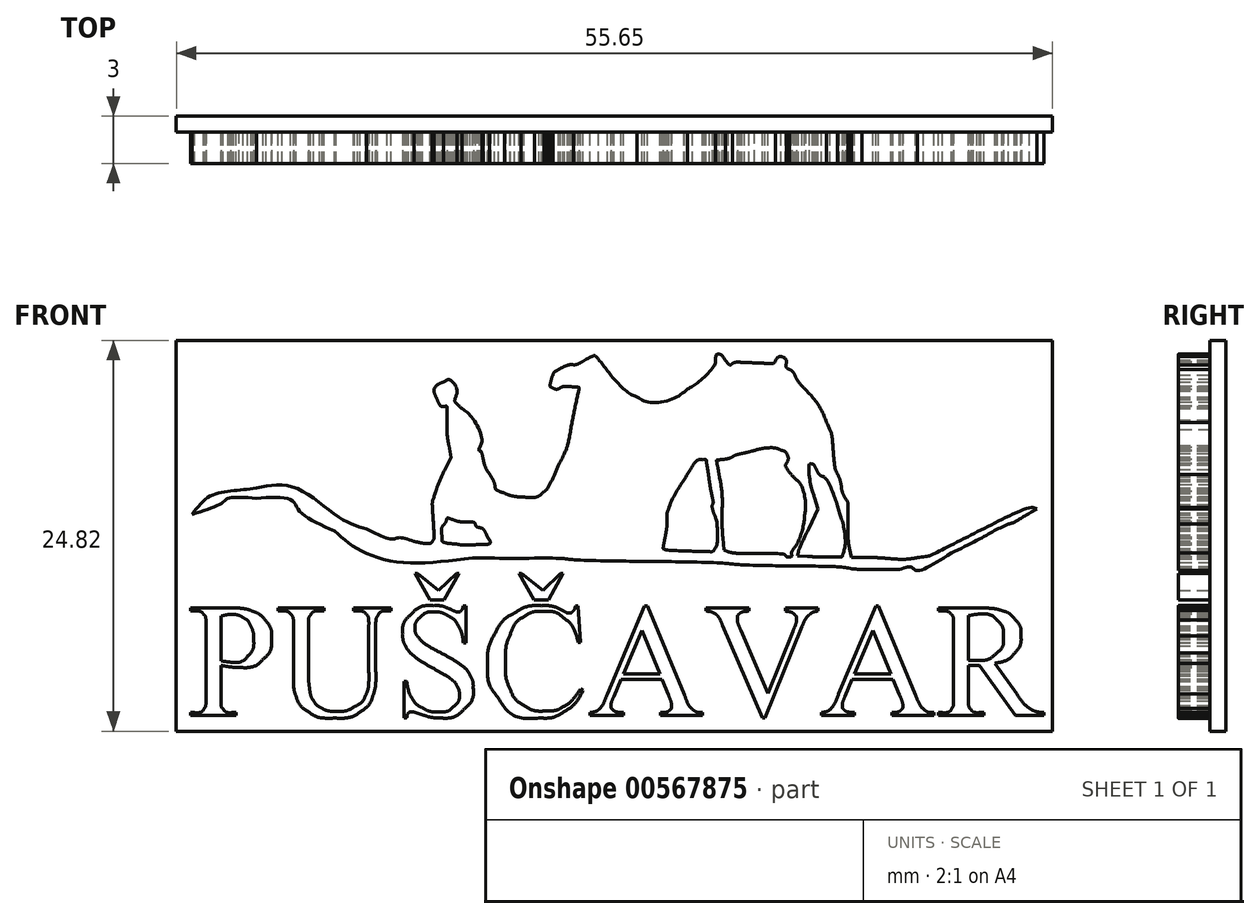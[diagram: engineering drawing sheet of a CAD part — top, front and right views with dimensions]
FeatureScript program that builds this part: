
annotation { "Feature Type Name" : "Feature", "Feature Type Description" : "" }
export const myFeature = defineFeature(function(context is Context, id is Id, definition is map)
    precondition{}
    {
        {
            var Q0;
            Q0=qCreatedBy(makeId("Front.planeOp"),FACE);
            var sketch = newSketch(context, id + "F0", { "sketchPlane" : qUnion([Q0])});
            skFitSpline(sketch, "E0", {"points": [v(-25.17, -10.13) * mm, v(-25.17, -10.56) * mm, v(-25.12, -10.83) * mm, v(-25.03, -10.93) * mm]});
            skFitSpline(sketch, "E1", {"points": [v(-25.03, -10.93) * mm, v(-24.9, -11.08) * mm, v(-24.72, -11.15) * mm, v(-24.46, -11.15) * mm]});
            skLineSegment(sketch, "E2", {"start": v(-25.17, -8.14) * mm, "end": v(-25.17, -10.13) * mm});
            skFitSpline(sketch, "E3", {"points": [v(-26.83, -11.15) * mm, v(-26.55, -11.15) * mm, v(-26.35, -11.06) * mm, v(-26.22, -10.87) * mm]});
            skFitSpline(sketch, "E4", {"points": [v(-26.22, -10.87) * mm, v(-26.16, -10.77) * mm, v(-26.12, -10.52) * mm, v(-26.12, -10.13) * mm]});
            skLineSegment(sketch, "E5", {"start": v(-24.46, -11.15) * mm, "end": v(-24.2, -11.15) * mm});
            skLineSegment(sketch, "E6", {"start": v(-24.2, -11.15) * mm, "end": v(-24.2, -11.34) * mm});
            skLineSegment(sketch, "E7", {"start": v(-24.2, -11.34) * mm, "end": v(-27.09, -11.34) * mm});
            skLineSegment(sketch, "E8", {"start": v(-27.09, -11.34) * mm, "end": v(-27.09, -11.15) * mm});
            skLineSegment(sketch, "E9", {"start": v(-27.09, -11.15) * mm, "end": v(-26.83, -11.15) * mm});
            skFitSpline(sketch, "E10", {"points": [v(-26.12, -5.72) * mm, v(-26.12, -5.3) * mm, v(-26.17, -5.03) * mm, v(-26.26, -4.93) * mm]});
            skFitSpline(sketch, "E11", {"points": [v(-26.26, -4.93) * mm, v(-26.39, -4.78) * mm, v(-26.58, -4.7) * mm, v(-26.83, -4.7) * mm]});
            skLineSegment(sketch, "E12", {"start": v(-26.12, -10.13) * mm, "end": v(-26.12, -5.72) * mm});
            skFitSpline(sketch, "E13", {"points": [v(-24.62, -4.52) * mm, v(-24.02, -4.52) * mm, v(-23.54, -4.58) * mm, v(-23.2, -4.7) * mm]});
            skFitSpline(sketch, "E14", {"points": [v(-23.2, -4.7) * mm, v(-22.85, -4.83) * mm, v(-22.56, -5.04) * mm, v(-22.32, -5.34) * mm]});
            skFitSpline(sketch, "E15", {"points": [v(-22.32, -5.34) * mm, v(-22.08, -5.64) * mm, v(-21.96, -6) * mm, v(-21.96, -6.4) * mm]});
            skFitSpline(sketch, "E16", {"points": [v(-21.96, -6.4) * mm, v(-21.96, -6.96) * mm, v(-22.14, -7.41) * mm, v(-22.5, -7.76) * mm]});
            skFitSpline(sketch, "E17", {"points": [v(-22.5, -7.76) * mm, v(-22.87, -8.11) * mm, v(-23.38, -8.29) * mm, v(-24.04, -8.29) * mm]});
            skFitSpline(sketch, "E18", {"points": [v(-24.04, -8.29) * mm, v(-24.2, -8.29) * mm, v(-24.38, -8.27) * mm, v(-24.57, -8.25) * mm]});
            skFitSpline(sketch, "E19", {"points": [v(-24.57, -8.25) * mm, v(-24.75, -8.23) * mm, v(-24.96, -8.2) * mm, v(-25.17, -8.14) * mm]});
            skLineSegment(sketch, "E20", {"start": v(-26.83, -4.7) * mm, "end": v(-27.09, -4.7) * mm});
            skLineSegment(sketch, "E21", {"start": v(-27.09, -4.7) * mm, "end": v(-27.09, -4.52) * mm});
            skLineSegment(sketch, "E22", {"start": v(-27.09, -4.52) * mm, "end": v(-24.62, -4.52) * mm});
            skFitSpline(sketch, "E23", {"points": [v(-25.17, -7.86) * mm, v(-25, -7.9) * mm, v(-24.84, -7.92) * mm, v(-24.7, -7.93) * mm]});
            skFitSpline(sketch, "E24", {"points": [v(-24.7, -7.93) * mm, v(-24.57, -7.95) * mm, v(-24.45, -7.96) * mm, v(-24.36, -7.96) * mm]});
            skFitSpline(sketch, "E25", {"points": [v(-24.36, -7.96) * mm, v(-24.01, -7.96) * mm, v(-23.72, -7.82) * mm, v(-23.47, -7.55) * mm]});
            skFitSpline(sketch, "E26", {"points": [v(-23.47, -7.55) * mm, v(-23.22, -7.28) * mm, v(-23.1, -6.93) * mm, v(-23.1, -6.5) * mm]});
            skFitSpline(sketch, "E27", {"points": [v(-23.1, -6.5) * mm, v(-23.1, -6.2) * mm, v(-23.15, -5.94) * mm, v(-23.27, -5.68) * mm]});
            skFitSpline(sketch, "E28", {"points": [v(-23.27, -5.68) * mm, v(-23.39, -5.43) * mm, v(-23.56, -5.24) * mm, v(-23.78, -5.11) * mm]});
            skFitSpline(sketch, "E29", {"points": [v(-23.78, -5.11) * mm, v(-24, -4.99) * mm, v(-24.24, -4.93) * mm, v(-24.52, -4.93) * mm]});
            skFitSpline(sketch, "E30", {"points": [v(-24.52, -4.93) * mm, v(-24.69, -4.93) * mm, v(-24.9, -4.96) * mm, v(-25.17, -5.02) * mm]});
            skLineSegment(sketch, "E31", {"start": v(-25.17, -5.02) * mm, "end": v(-25.17, -7.86) * mm});
            skFitSpline(sketch, "E32", {"points": [v(-14.62, -4.7) * mm, v(-14.89, -4.7) * mm, v(-15.1, -4.82) * mm, v(-15.23, -5.04) * mm]});
            skFitSpline(sketch, "E33", {"points": [v(-15.23, -5.04) * mm, v(-15.3, -5.14) * mm, v(-15.34, -5.39) * mm, v(-15.34, -5.77) * mm]});
            skLineSegment(sketch, "E34", {"start": v(-16.75, -4.7) * mm, "end": v(-16.75, -4.52) * mm});
            skLineSegment(sketch, "E35", {"start": v(-16.75, -4.52) * mm, "end": v(-14.37, -4.52) * mm});
            skLineSegment(sketch, "E36", {"start": v(-14.37, -4.52) * mm, "end": v(-14.37, -4.7) * mm});
            skLineSegment(sketch, "E37", {"start": v(-14.37, -4.7) * mm, "end": v(-14.62, -4.7) * mm});
            skFitSpline(sketch, "E38", {"points": [v(-15.34, -8.53) * mm, v(-15.34, -9.22) * mm, v(-15.4, -9.75) * mm, v(-15.54, -10.12) * mm]});
            skFitSpline(sketch, "E39", {"points": [v(-15.54, -10.12) * mm, v(-15.67, -10.5) * mm, v(-15.93, -10.82) * mm, v(-16.33, -11.1) * mm]});
            skFitSpline(sketch, "E40", {"points": [v(-16.33, -11.1) * mm, v(-16.72, -11.36) * mm, v(-17.25, -11.5) * mm, v(-17.93, -11.5) * mm]});
            skFitSpline(sketch, "E41", {"points": [v(-17.93, -11.5) * mm, v(-18.66, -11.5) * mm, v(-19.22, -11.37) * mm, v(-19.6, -11.11) * mm]});
            skFitSpline(sketch, "E42", {"points": [v(-19.6, -11.11) * mm, v(-19.98, -10.85) * mm, v(-20.25, -10.5) * mm, v(-20.4, -10.07) * mm]});
            skFitSpline(sketch, "E43", {"points": [v(-20.4, -10.07) * mm, v(-20.51, -9.77) * mm, v(-20.57, -9.21) * mm, v(-20.57, -8.4) * mm]});
            skLineSegment(sketch, "E44", {"start": v(-15.34, -5.77) * mm, "end": v(-15.34, -8.53) * mm});
            skFitSpline(sketch, "E45", {"points": [v(-20.57, -5.72) * mm, v(-20.57, -5.3) * mm, v(-20.62, -5.03) * mm, v(-20.74, -4.9) * mm]});
            skFitSpline(sketch, "E46", {"points": [v(-20.74, -4.9) * mm, v(-20.85, -4.77) * mm, v(-21.04, -4.7) * mm, v(-21.3, -4.7) * mm]});
            skLineSegment(sketch, "E47", {"start": v(-20.57, -8.4) * mm, "end": v(-20.57, -5.72) * mm});
            skFitSpline(sketch, "E48", {"points": [v(-18.9, -4.7) * mm, v(-19.17, -4.7) * mm, v(-19.37, -4.8) * mm, v(-19.49, -4.97) * mm]});
            skFitSpline(sketch, "E49", {"points": [v(-19.49, -4.97) * mm, v(-19.57, -5.1) * mm, v(-19.61, -5.34) * mm, v(-19.61, -5.72) * mm]});
            skLineSegment(sketch, "E50", {"start": v(-21.3, -4.7) * mm, "end": v(-21.54, -4.7) * mm});
            skLineSegment(sketch, "E51", {"start": v(-21.54, -4.7) * mm, "end": v(-21.54, -4.52) * mm});
            skLineSegment(sketch, "E52", {"start": v(-21.54, -4.52) * mm, "end": v(-18.64, -4.52) * mm});
            skLineSegment(sketch, "E53", {"start": v(-18.64, -4.52) * mm, "end": v(-18.64, -4.7) * mm});
            skLineSegment(sketch, "E54", {"start": v(-18.64, -4.7) * mm, "end": v(-18.9, -4.7) * mm});
            skFitSpline(sketch, "E55", {"points": [v(-19.61, -8.7) * mm, v(-19.61, -8.96) * mm, v(-19.59, -9.27) * mm, v(-19.54, -9.6) * mm]});
            skFitSpline(sketch, "E56", {"points": [v(-19.54, -9.6) * mm, v(-19.5, -9.95) * mm, v(-19.4, -10.22) * mm, v(-19.28, -10.4) * mm]});
            skFitSpline(sketch, "E57", {"points": [v(-19.28, -10.4) * mm, v(-19.16, -10.6) * mm, v(-18.97, -10.76) * mm, v(-18.74, -10.88) * mm]});
            skFitSpline(sketch, "E58", {"points": [v(-18.74, -10.88) * mm, v(-18.5, -11) * mm, v(-18.21, -11.07) * mm, v(-17.87, -11.07) * mm]});
            skFitSpline(sketch, "E59", {"points": [v(-17.87, -11.07) * mm, v(-17.43, -11.07) * mm, v(-17.03, -10.97) * mm, v(-16.69, -10.78) * mm]});
            skFitSpline(sketch, "E60", {"points": [v(-16.69, -10.78) * mm, v(-16.34, -10.58) * mm, v(-16.1, -10.33) * mm, v(-15.97, -10.03) * mm]});
            skFitSpline(sketch, "E61", {"points": [v(-15.97, -10.03) * mm, v(-15.85, -9.72) * mm, v(-15.78, -9.21) * mm, v(-15.78, -8.49) * mm]});
            skLineSegment(sketch, "E62", {"start": v(-19.61, -5.72) * mm, "end": v(-19.61, -8.7) * mm});
            skFitSpline(sketch, "E63", {"points": [v(-15.78, -5.72) * mm, v(-15.78, -5.3) * mm, v(-15.83, -5.03) * mm, v(-15.92, -4.93) * mm]});
            skFitSpline(sketch, "E64", {"points": [v(-15.92, -4.93) * mm, v(-16.05, -4.78) * mm, v(-16.24, -4.7) * mm, v(-16.5, -4.7) * mm]});
            skLineSegment(sketch, "E65", {"start": v(-15.78, -8.49) * mm, "end": v(-15.78, -5.72) * mm});
            skLineSegment(sketch, "E66", {"start": v(-16.5, -4.7) * mm, "end": v(-16.75, -4.7) * mm});
            skFitSpline(sketch, "E67", {"points": [v(-9.78, -6.72) * mm, v(-9.84, -6.27) * mm, v(-9.95, -5.9) * mm, v(-10.1, -5.64) * mm]});
            skFitSpline(sketch, "E68", {"points": [v(-10.1, -5.64) * mm, v(-10.25, -5.37) * mm, v(-10.47, -5.16) * mm, v(-10.76, -5) * mm]});
            skFitSpline(sketch, "E69", {"points": [v(-10.76, -5) * mm, v(-11.04, -4.84) * mm, v(-11.34, -4.76) * mm, v(-11.64, -4.76) * mm]});
            skFitSpline(sketch, "E70", {"points": [v(-11.64, -4.76) * mm, v(-11.98, -4.76) * mm, v(-12.27, -4.87) * mm, v(-12.5, -5.08) * mm]});
            skFitSpline(sketch, "E71", {"points": [v(-12.5, -5.08) * mm, v(-12.72, -5.3) * mm, v(-12.83, -5.54) * mm, v(-12.83, -5.81) * mm]});
            skFitSpline(sketch, "E72", {"points": [v(-12.83, -5.81) * mm, v(-12.83, -6.02) * mm, v(-12.76, -6.2) * mm, v(-12.62, -6.38) * mm]});
            skFitSpline(sketch, "E73", {"points": [v(-12.62, -6.38) * mm, v(-12.41, -6.63) * mm, v(-11.92, -6.97) * mm, v(-11.15, -7.38) * mm]});
            skFitSpline(sketch, "E74", {"points": [v(-11.15, -7.38) * mm, v(-10.53, -7.73) * mm, v(-10.1, -7.99) * mm, v(-9.87, -8.17) * mm]});
            skFitSpline(sketch, "E75", {"points": [v(-9.87, -8.17) * mm, v(-9.64, -8.36) * mm, v(-9.46, -8.57) * mm, v(-9.34, -8.82) * mm]});
            skFitSpline(sketch, "E76", {"points": [v(-9.34, -8.82) * mm, v(-9.21, -9.07) * mm, v(-9.15, -9.33) * mm, v(-9.15, -9.6) * mm]});
            skFitSpline(sketch, "E77", {"points": [v(-9.15, -9.6) * mm, v(-9.15, -10.11) * mm, v(-9.35, -10.56) * mm, v(-9.74, -10.93) * mm]});
            skFitSpline(sketch, "E78", {"points": [v(-9.74, -10.93) * mm, v(-10.14, -11.3) * mm, v(-10.65, -11.5) * mm, v(-11.27, -11.5) * mm]});
            skFitSpline(sketch, "E79", {"points": [v(-11.27, -11.5) * mm, v(-11.46, -11.5) * mm, v(-11.65, -11.48) * mm, v(-11.82, -11.45) * mm]});
            skFitSpline(sketch, "E80", {"points": [v(-11.82, -11.45) * mm, v(-11.92, -11.43) * mm, v(-12.13, -11.37) * mm, v(-12.46, -11.27) * mm]});
            skFitSpline(sketch, "E81", {"points": [v(-12.46, -11.27) * mm, v(-12.78, -11.16) * mm, v(-12.98, -11.1) * mm, v(-13.07, -11.1) * mm]});
            skFitSpline(sketch, "E82", {"points": [v(-13.07, -11.1) * mm, v(-13.15, -11.1) * mm, v(-13.22, -11.13) * mm, v(-13.27, -11.18) * mm]});
            skFitSpline(sketch, "E83", {"points": [v(-13.27, -11.18) * mm, v(-13.31, -11.23) * mm, v(-13.35, -11.34) * mm, v(-13.37, -11.5) * mm]});
            skLineSegment(sketch, "E84", {"start": v(-9.6, -4.36) * mm, "end": v(-9.6, -6.72) * mm});
            skLineSegment(sketch, "E85", {"start": v(-9.6, -6.72) * mm, "end": v(-9.78, -6.72) * mm});
            skFitSpline(sketch, "E86", {"points": [v(-13.37, -9.16) * mm, v(-13.29, -9.65) * mm, v(-13.17, -10.01) * mm, v(-13.02, -10.25) * mm]});
            skFitSpline(sketch, "E87", {"points": [v(-13.02, -10.25) * mm, v(-12.88, -10.5) * mm, v(-12.66, -10.7) * mm, v(-12.36, -10.86) * mm]});
            skFitSpline(sketch, "E88", {"points": [v(-12.36, -10.86) * mm, v(-12.06, -11.02) * mm, v(-11.73, -11.1) * mm, v(-11.37, -11.1) * mm]});
            skFitSpline(sketch, "E89", {"points": [v(-11.37, -11.1) * mm, v(-10.96, -11.1) * mm, v(-10.63, -11) * mm, v(-10.4, -10.77) * mm]});
            skFitSpline(sketch, "E90", {"points": [v(-10.4, -10.77) * mm, v(-10.15, -10.55) * mm, v(-10.03, -10.29) * mm, v(-10.03, -9.99) * mm]});
            skFitSpline(sketch, "E91", {"points": [v(-10.03, -9.99) * mm, v(-10.03, -9.82) * mm, v(-10.08, -9.65) * mm, v(-10.17, -9.48) * mm]});
            skFitSpline(sketch, "E92", {"points": [v(-10.17, -9.48) * mm, v(-10.26, -9.3) * mm, v(-10.4, -9.15) * mm, v(-10.6, -9) * mm]});
            skFitSpline(sketch, "E93", {"points": [v(-10.6, -9) * mm, v(-10.72, -8.9) * mm, v(-11.07, -8.69) * mm, v(-11.65, -8.36) * mm]});
            skFitSpline(sketch, "E94", {"points": [v(-11.65, -8.36) * mm, v(-12.23, -8.03) * mm, v(-12.64, -7.77) * mm, v(-12.88, -7.58) * mm]});
            skFitSpline(sketch, "E95", {"points": [v(-12.88, -7.58) * mm, v(-13.12, -7.38) * mm, v(-13.3, -7.17) * mm, v(-13.43, -6.93) * mm]});
            skFitSpline(sketch, "E96", {"points": [v(-13.43, -6.93) * mm, v(-13.56, -6.7) * mm, v(-13.62, -6.44) * mm, v(-13.62, -6.16) * mm]});
            skFitSpline(sketch, "E97", {"points": [v(-13.62, -6.16) * mm, v(-13.62, -5.67) * mm, v(-13.43, -5.25) * mm, v(-13.06, -4.9) * mm]});
            skFitSpline(sketch, "E98", {"points": [v(-13.06, -4.9) * mm, v(-12.7, -4.54) * mm, v(-12.22, -4.36) * mm, v(-11.65, -4.36) * mm]});
            skFitSpline(sketch, "E99", {"points": [v(-11.65, -4.36) * mm, v(-11.3, -4.36) * mm, v(-10.91, -4.45) * mm, v(-10.51, -4.63) * mm]});
            skFitSpline(sketch, "E100", {"points": [v(-10.51, -4.63) * mm, v(-10.33, -4.71) * mm, v(-10.2, -4.75) * mm, v(-10.12, -4.75) * mm]});
            skFitSpline(sketch, "E101", {"points": [v(-10.12, -4.75) * mm, v(-10.04, -4.75) * mm, v(-9.97, -4.73) * mm, v(-9.91, -4.68) * mm]});
            skFitSpline(sketch, "E102", {"points": [v(-9.91, -4.68) * mm, v(-9.86, -4.62) * mm, v(-9.81, -4.52) * mm, v(-9.78, -4.36) * mm]});
            skLineSegment(sketch, "E103", {"start": v(-13.37, -11.5) * mm, "end": v(-13.56, -11.5) * mm});
            skLineSegment(sketch, "E104", {"start": v(-13.56, -11.5) * mm, "end": v(-13.56, -9.16) * mm});
            skLineSegment(sketch, "E105", {"start": v(-13.56, -9.16) * mm, "end": v(-13.37, -9.16) * mm});
            skLineSegment(sketch, "E106", {"start": v(-9.78, -4.36) * mm, "end": v(-9.6, -4.36) * mm});
            skLineSegment(sketch, "E107", {"start": v(-11, -3.98) * mm, "end": v(-11.9, -3.98) * mm});
            skLineSegment(sketch, "E108", {"start": v(-11.9, -3.98) * mm, "end": v(-12.85, -2.32) * mm});
            skLineSegment(sketch, "E109", {"start": v(-12.85, -2.32) * mm, "end": v(-12.7, -2.32) * mm});
            skLineSegment(sketch, "E110", {"start": v(-12.7, -2.32) * mm, "end": v(-11.34, -3.39) * mm});
            skLineSegment(sketch, "E111", {"start": v(-11.34, -3.39) * mm, "end": v(-10.2, -2.32) * mm});
            skLineSegment(sketch, "E112", {"start": v(-10.2, -2.32) * mm, "end": v(-10.05, -2.32) * mm});
            skLineSegment(sketch, "E113", {"start": v(-10.05, -2.32) * mm, "end": v(-11, -3.98) * mm});
            skFitSpline(sketch, "E114", {"points": [v(-2.48, -6.68) * mm, v(-2.69, -5.99) * mm, v(-2.98, -5.49) * mm, v(-3.36, -5.18) * mm]});
            skFitSpline(sketch, "E115", {"points": [v(-3.36, -5.18) * mm, v(-3.74, -4.88) * mm, v(-4.2, -4.72) * mm, v(-4.73, -4.72) * mm]});
            skFitSpline(sketch, "E116", {"points": [v(-4.73, -4.72) * mm, v(-5.18, -4.72) * mm, v(-5.58, -4.84) * mm, v(-5.94, -5.07) * mm]});
            skFitSpline(sketch, "E117", {"points": [v(-5.94, -5.07) * mm, v(-6.3, -5.3) * mm, v(-6.58, -5.66) * mm, v(-6.8, -6.17) * mm]});
            skFitSpline(sketch, "E118", {"points": [v(-6.8, -6.17) * mm, v(-7, -6.67) * mm, v(-7.1, -7.3) * mm, v(-7.1, -8.04) * mm]});
            skFitSpline(sketch, "E119", {"points": [v(-7.1, -8.04) * mm, v(-7.1, -8.66) * mm, v(-7, -9.2) * mm, v(-6.8, -9.65) * mm]});
            skFitSpline(sketch, "E120", {"points": [v(-6.8, -9.65) * mm, v(-6.61, -10.1) * mm, v(-6.32, -10.45) * mm, v(-5.93, -10.7) * mm]});
            skFitSpline(sketch, "E121", {"points": [v(-5.93, -10.7) * mm, v(-5.53, -10.93) * mm, v(-5.09, -11.05) * mm, v(-4.58, -11.05) * mm]});
            skFitSpline(sketch, "E122", {"points": [v(-4.58, -11.05) * mm, v(-4.15, -11.05) * mm, v(-3.76, -10.96) * mm, v(-3.43, -10.77) * mm]});
            skFitSpline(sketch, "E123", {"points": [v(-3.43, -10.77) * mm, v(-3.1, -10.58) * mm, v(-2.73, -10.2) * mm, v(-2.33, -9.64) * mm]});
            skLineSegment(sketch, "E124", {"start": v(-2.48, -4.36) * mm, "end": v(-2.33, -6.68) * mm});
            skLineSegment(sketch, "E125", {"start": v(-2.33, -6.68) * mm, "end": v(-2.48, -6.68) * mm});
            skFitSpline(sketch, "E126", {"points": [v(-2.17, -9.74) * mm, v(-2.51, -10.35) * mm, v(-2.9, -10.8) * mm, v(-3.35, -11.07) * mm]});
            skFitSpline(sketch, "E127", {"points": [v(-3.35, -11.07) * mm, v(-3.8, -11.35) * mm, v(-4.34, -11.5) * mm, v(-4.96, -11.5) * mm]});
            skFitSpline(sketch, "E128", {"points": [v(-4.96, -11.5) * mm, v(-6.07, -11.5) * mm, v(-6.93, -11.08) * mm, v(-7.55, -10.24) * mm]});
            skFitSpline(sketch, "E129", {"points": [v(-7.55, -10.24) * mm, v(-8, -9.61) * mm, v(-8.23, -8.88) * mm, v(-8.23, -8.03) * mm]});
            skFitSpline(sketch, "E130", {"points": [v(-8.23, -8.03) * mm, v(-8.23, -7.35) * mm, v(-8.08, -6.73) * mm, v(-7.78, -6.16) * mm]});
            skFitSpline(sketch, "E131", {"points": [v(-7.78, -6.16) * mm, v(-7.48, -5.59) * mm, v(-7.06, -5.15) * mm, v(-6.54, -4.83) * mm]});
            skFitSpline(sketch, "E132", {"points": [v(-6.54, -4.83) * mm, v(-6, -4.52) * mm, v(-5.43, -4.36) * mm, v(-4.8, -4.36) * mm]});
            skFitSpline(sketch, "E133", {"points": [v(-4.8, -4.36) * mm, v(-4.32, -4.36) * mm, v(-3.84, -4.48) * mm, v(-3.37, -4.72) * mm]});
            skFitSpline(sketch, "E134", {"points": [v(-3.37, -4.72) * mm, v(-3.23, -4.8) * mm, v(-3.13, -4.83) * mm, v(-3.07, -4.83) * mm]});
            skFitSpline(sketch, "E135", {"points": [v(-3.07, -4.83) * mm, v(-2.98, -4.83) * mm, v(-2.9, -4.8) * mm, v(-2.84, -4.74) * mm]});
            skFitSpline(sketch, "E136", {"points": [v(-2.84, -4.74) * mm, v(-2.75, -4.65) * mm, v(-2.7, -4.52) * mm, v(-2.65, -4.36) * mm]});
            skLineSegment(sketch, "E137", {"start": v(-2.33, -9.64) * mm, "end": v(-2.17, -9.74) * mm});
            skLineSegment(sketch, "E138", {"start": v(-2.65, -4.36) * mm, "end": v(-2.48, -4.36) * mm});
            skLineSegment(sketch, "E139", {"start": v(-4.38, -3.98) * mm, "end": v(-5.3, -3.98) * mm});
            skLineSegment(sketch, "E140", {"start": v(-5.3, -3.98) * mm, "end": v(-6.24, -2.32) * mm});
            skLineSegment(sketch, "E141", {"start": v(-6.24, -2.32) * mm, "end": v(-6.08, -2.32) * mm});
            skLineSegment(sketch, "E142", {"start": v(-6.08, -2.32) * mm, "end": v(-4.73, -3.39) * mm});
            skLineSegment(sketch, "E143", {"start": v(-4.73, -3.39) * mm, "end": v(-3.6, -2.32) * mm});
            skLineSegment(sketch, "E144", {"start": v(-3.6, -2.32) * mm, "end": v(-3.44, -2.32) * mm});
            skLineSegment(sketch, "E145", {"start": v(-3.44, -2.32) * mm, "end": v(-4.38, -3.98) * mm});
            skFitSpline(sketch, "E146", {"points": [v(-0.22, -10.13) * mm, v(-0.34, -10.4) * mm, v(-0.4, -10.6) * mm, v(-0.4, -10.73) * mm]});
            skFitSpline(sketch, "E147", {"points": [v(-0.4, -10.73) * mm, v(-0.4, -10.83) * mm, v(-0.34, -10.92) * mm, v(-0.25, -11) * mm]});
            skFitSpline(sketch, "E148", {"points": [v(-0.25, -11) * mm, v(-0.15, -11.08) * mm, v(0.06, -11.13) * mm, v(0.39, -11.15) * mm]});
            skLineSegment(sketch, "E149", {"start": v(2.84, -9.06) * mm, "end": v(0.23, -9.06) * mm});
            skLineSegment(sketch, "E150", {"start": v(0.23, -9.06) * mm, "end": v(-0.22, -10.13) * mm});
            skFitSpline(sketch, "E151", {"points": [v(-1.73, -11.15) * mm, v(-1.45, -11.1) * mm, v(-1.27, -11.04) * mm, v(-1.19, -10.96) * mm]});
            skFitSpline(sketch, "E152", {"points": [v(-1.19, -10.96) * mm, v(-1.02, -10.8) * mm, v(-0.83, -10.47) * mm, v(-0.63, -9.98) * mm]});
            skLineSegment(sketch, "E153", {"start": v(0.39, -11.15) * mm, "end": v(0.39, -11.34) * mm});
            skLineSegment(sketch, "E154", {"start": v(0.39, -11.34) * mm, "end": v(-1.73, -11.34) * mm});
            skLineSegment(sketch, "E155", {"start": v(-1.73, -11.34) * mm, "end": v(-1.73, -11.15) * mm});
            skFitSpline(sketch, "E156", {"points": [v(4.26, -10.04) * mm, v(4.45, -10.5) * mm, v(4.62, -10.79) * mm, v(4.77, -10.92) * mm]});
            skFitSpline(sketch, "E157", {"points": [v(4.77, -10.92) * mm, v(4.92, -11.06) * mm, v(5.14, -11.14) * mm, v(5.41, -11.15) * mm]});
            skLineSegment(sketch, "E158", {"start": v(-0.63, -9.98) * mm, "end": v(1.74, -4.36) * mm});
            skLineSegment(sketch, "E159", {"start": v(1.74, -4.36) * mm, "end": v(1.92, -4.36) * mm});
            skLineSegment(sketch, "E160", {"start": v(1.92, -4.36) * mm, "end": v(4.26, -10.04) * mm});
            skFitSpline(sketch, "E161", {"points": [v(2.76, -11.15) * mm, v(3.03, -11.14) * mm, v(3.2, -11.1) * mm, v(3.3, -11.02) * mm]});
            skFitSpline(sketch, "E162", {"points": [v(3.3, -11.02) * mm, v(3.4, -10.94) * mm, v(3.44, -10.85) * mm, v(3.44, -10.74) * mm]});
            skFitSpline(sketch, "E163", {"points": [v(3.44, -10.74) * mm, v(3.44, -10.59) * mm, v(3.38, -10.35) * mm, v(3.24, -10.04) * mm]});
            skLineSegment(sketch, "E164", {"start": v(5.41, -11.15) * mm, "end": v(5.41, -11.34) * mm});
            skLineSegment(sketch, "E165", {"start": v(5.41, -11.34) * mm, "end": v(2.76, -11.34) * mm});
            skLineSegment(sketch, "E166", {"start": v(2.76, -11.34) * mm, "end": v(2.76, -11.15) * mm});
            skLineSegment(sketch, "E167", {"start": v(3.24, -10.04) * mm, "end": v(2.84, -9.06) * mm});
            skLineSegment(sketch, "E168", {"start": v(2.7, -8.68) * mm, "end": v(1.56, -5.93) * mm});
            skLineSegment(sketch, "E169", {"start": v(1.56, -5.93) * mm, "end": v(0.39, -8.68) * mm});
            skLineSegment(sketch, "E170", {"start": v(0.39, -8.68) * mm, "end": v(2.7, -8.68) * mm});
            skFitSpline(sketch, "E171", {"points": [v(12.75, -4.7) * mm, v(12.5, -4.75) * mm, v(12.33, -4.82) * mm, v(12.2, -4.94) * mm]});
            skFitSpline(sketch, "E172", {"points": [v(12.2, -4.94) * mm, v(12.03, -5.1) * mm, v(11.88, -5.35) * mm, v(11.74, -5.69) * mm]});
            skLineSegment(sketch, "E173", {"start": v(12.75, -4.52) * mm, "end": v(12.75, -4.7) * mm});
            skFitSpline(sketch, "E174", {"points": [v(6.69, -5.61) * mm, v(6.56, -5.31) * mm, v(6.47, -5.13) * mm, v(6.42, -5.06) * mm]});
            skFitSpline(sketch, "E175", {"points": [v(6.42, -5.06) * mm, v(6.33, -4.96) * mm, v(6.23, -4.88) * mm, v(6.11, -4.82) * mm]});
            skFitSpline(sketch, "E176", {"points": [v(6.11, -4.82) * mm, v(5.99, -4.76) * mm, v(5.83, -4.72) * mm, v(5.62, -4.7) * mm]});
            skLineSegment(sketch, "E177", {"start": v(11.74, -5.69) * mm, "end": v(9.4, -11.5) * mm});
            skLineSegment(sketch, "E178", {"start": v(9.4, -11.5) * mm, "end": v(9.2, -11.5) * mm});
            skLineSegment(sketch, "E179", {"start": v(9.2, -11.5) * mm, "end": v(6.69, -5.61) * mm});
            skFitSpline(sketch, "E180", {"points": [v(8.37, -4.7) * mm, v(8.06, -4.73) * mm, v(7.86, -4.79) * mm, v(7.77, -4.86) * mm]});
            skFitSpline(sketch, "E181", {"points": [v(7.77, -4.86) * mm, v(7.67, -4.94) * mm, v(7.63, -5.04) * mm, v(7.63, -5.16) * mm]});
            skFitSpline(sketch, "E182", {"points": [v(7.63, -5.16) * mm, v(7.63, -5.33) * mm, v(7.7, -5.6) * mm, v(7.85, -5.95) * mm]});
            skLineSegment(sketch, "E183", {"start": v(5.62, -4.7) * mm, "end": v(5.62, -4.52) * mm});
            skLineSegment(sketch, "E184", {"start": v(5.62, -4.52) * mm, "end": v(8.37, -4.52) * mm});
            skLineSegment(sketch, "E185", {"start": v(8.37, -4.52) * mm, "end": v(8.37, -4.7) * mm});
            skFitSpline(sketch, "E186", {"points": [v(11.15, -6) * mm, v(11.3, -5.6) * mm, v(11.39, -5.34) * mm, v(11.39, -5.19) * mm]});
            skFitSpline(sketch, "E187", {"points": [v(11.39, -5.19) * mm, v(11.39, -5.09) * mm, v(11.34, -5) * mm, v(11.24, -4.9) * mm]});
            skFitSpline(sketch, "E188", {"points": [v(11.24, -4.9) * mm, v(11.15, -4.82) * mm, v(10.99, -4.76) * mm, v(10.76, -4.72) * mm]});
            skFitSpline(sketch, "E189", {"points": [v(10.76, -4.72) * mm, v(10.74, -4.72) * mm, v(10.71, -4.71) * mm, v(10.67, -4.7) * mm]});
            skLineSegment(sketch, "E190", {"start": v(7.85, -5.95) * mm, "end": v(9.57, -9.95) * mm});
            skLineSegment(sketch, "E191", {"start": v(9.57, -9.95) * mm, "end": v(11.15, -6) * mm});
            skLineSegment(sketch, "E192", {"start": v(10.67, -4.7) * mm, "end": v(10.67, -4.52) * mm});
            skLineSegment(sketch, "E193", {"start": v(10.67, -4.52) * mm, "end": v(12.75, -4.52) * mm});
            skFitSpline(sketch, "E194", {"points": [v(14.46, -10.13) * mm, v(14.35, -10.4) * mm, v(14.3, -10.6) * mm, v(14.3, -10.73) * mm]});
            skFitSpline(sketch, "E195", {"points": [v(14.3, -10.73) * mm, v(14.3, -10.83) * mm, v(14.34, -10.92) * mm, v(14.44, -11) * mm]});
            skFitSpline(sketch, "E196", {"points": [v(14.44, -11) * mm, v(14.54, -11.08) * mm, v(14.75, -11.13) * mm, v(15.07, -11.15) * mm]});
            skLineSegment(sketch, "E197", {"start": v(17.52, -9.06) * mm, "end": v(14.92, -9.06) * mm});
            skLineSegment(sketch, "E198", {"start": v(14.92, -9.06) * mm, "end": v(14.46, -10.13) * mm});
            skFitSpline(sketch, "E199", {"points": [v(12.96, -11.15) * mm, v(13.24, -11.1) * mm, v(13.42, -11.04) * mm, v(13.5, -10.96) * mm]});
            skFitSpline(sketch, "E200", {"points": [v(13.5, -10.96) * mm, v(13.67, -10.8) * mm, v(13.86, -10.47) * mm, v(14.06, -9.98) * mm]});
            skLineSegment(sketch, "E201", {"start": v(15.07, -11.15) * mm, "end": v(15.07, -11.34) * mm});
            skLineSegment(sketch, "E202", {"start": v(15.07, -11.34) * mm, "end": v(12.96, -11.34) * mm});
            skLineSegment(sketch, "E203", {"start": v(12.96, -11.34) * mm, "end": v(12.96, -11.15) * mm});
            skFitSpline(sketch, "E204", {"points": [v(18.94, -10.04) * mm, v(19.13, -10.5) * mm, v(19.3, -10.79) * mm, v(19.46, -10.92) * mm]});
            skFitSpline(sketch, "E205", {"points": [v(19.46, -10.92) * mm, v(19.61, -11.06) * mm, v(19.83, -11.14) * mm, v(20.1, -11.15) * mm]});
            skLineSegment(sketch, "E206", {"start": v(14.06, -9.98) * mm, "end": v(16.43, -4.36) * mm});
            skLineSegment(sketch, "E207", {"start": v(16.43, -4.36) * mm, "end": v(16.6, -4.36) * mm});
            skLineSegment(sketch, "E208", {"start": v(16.6, -4.36) * mm, "end": v(18.94, -10.04) * mm});
            skFitSpline(sketch, "E209", {"points": [v(17.45, -11.15) * mm, v(17.71, -11.14) * mm, v(17.9, -11.1) * mm, v(17.99, -11.02) * mm]});
            skFitSpline(sketch, "E210", {"points": [v(17.99, -11.02) * mm, v(18.08, -10.94) * mm, v(18.13, -10.85) * mm, v(18.13, -10.74) * mm]});
            skFitSpline(sketch, "E211", {"points": [v(18.13, -10.74) * mm, v(18.13, -10.59) * mm, v(18.06, -10.35) * mm, v(17.93, -10.04) * mm]});
            skLineSegment(sketch, "E212", {"start": v(20.1, -11.15) * mm, "end": v(20.1, -11.34) * mm});
            skLineSegment(sketch, "E213", {"start": v(20.1, -11.34) * mm, "end": v(17.45, -11.34) * mm});
            skLineSegment(sketch, "E214", {"start": v(17.45, -11.34) * mm, "end": v(17.45, -11.15) * mm});
            skLineSegment(sketch, "E215", {"start": v(17.93, -10.04) * mm, "end": v(17.52, -9.06) * mm});
            skLineSegment(sketch, "E216", {"start": v(17.39, -8.68) * mm, "end": v(16.24, -5.93) * mm});
            skLineSegment(sketch, "E217", {"start": v(16.24, -5.93) * mm, "end": v(15.07, -8.68) * mm});
            skLineSegment(sketch, "E218", {"start": v(15.07, -8.68) * mm, "end": v(17.39, -8.68) * mm});
            skFitSpline(sketch, "E219", {"points": [v(23.01, -8.15) * mm, v(22.84, -8.16) * mm, v(22.7, -8.16) * mm, v(22.6, -8.16) * mm]});
            skFitSpline(sketch, "E220", {"points": [v(22.6, -8.16) * mm, v(22.56, -8.16) * mm, v(22.51, -8.16) * mm, v(22.46, -8.16) * mm]});
            skFitSpline(sketch, "E221", {"points": [v(22.46, -8.16) * mm, v(22.41, -8.16) * mm, v(22.36, -8.15) * mm, v(22.3, -8.15) * mm]});
            skLineSegment(sketch, "E222", {"start": v(27.09, -11.34) * mm, "end": v(25.29, -11.34) * mm});
            skLineSegment(sketch, "E223", {"start": v(25.29, -11.34) * mm, "end": v(23.01, -8.15) * mm});
            skFitSpline(sketch, "E224", {"points": [v(22.3, -10.13) * mm, v(22.3, -10.56) * mm, v(22.35, -10.83) * mm, v(22.45, -10.93) * mm]});
            skFitSpline(sketch, "E225", {"points": [v(22.45, -10.93) * mm, v(22.57, -11.08) * mm, v(22.76, -11.15) * mm, v(23.01, -11.15) * mm]});
            skLineSegment(sketch, "E226", {"start": v(22.3, -8.15) * mm, "end": v(22.3, -10.13) * mm});
            skFitSpline(sketch, "E227", {"points": [v(20.65, -11.15) * mm, v(20.93, -11.15) * mm, v(21.13, -11.06) * mm, v(21.26, -10.87) * mm]});
            skFitSpline(sketch, "E228", {"points": [v(21.26, -10.87) * mm, v(21.33, -10.77) * mm, v(21.36, -10.52) * mm, v(21.36, -10.13) * mm]});
            skLineSegment(sketch, "E229", {"start": v(23.01, -11.15) * mm, "end": v(23.28, -11.15) * mm});
            skLineSegment(sketch, "E230", {"start": v(23.28, -11.15) * mm, "end": v(23.28, -11.34) * mm});
            skLineSegment(sketch, "E231", {"start": v(23.28, -11.34) * mm, "end": v(20.4, -11.34) * mm});
            skLineSegment(sketch, "E232", {"start": v(20.4, -11.34) * mm, "end": v(20.4, -11.15) * mm});
            skLineSegment(sketch, "E233", {"start": v(20.4, -11.15) * mm, "end": v(20.65, -11.15) * mm});
            skFitSpline(sketch, "E234", {"points": [v(21.36, -5.72) * mm, v(21.36, -5.3) * mm, v(21.31, -5.03) * mm, v(21.22, -4.92) * mm]});
            skFitSpline(sketch, "E235", {"points": [v(21.22, -4.92) * mm, v(21.1, -4.78) * mm, v(20.9, -4.7) * mm, v(20.65, -4.7) * mm]});
            skLineSegment(sketch, "E236", {"start": v(21.36, -10.13) * mm, "end": v(21.36, -5.72) * mm});
            skFitSpline(sketch, "E237", {"points": [v(22.84, -4.52) * mm, v(23.56, -4.52) * mm, v(24.09, -4.57) * mm, v(24.42, -4.68) * mm]});
            skFitSpline(sketch, "E238", {"points": [v(24.42, -4.68) * mm, v(24.76, -4.78) * mm, v(25.05, -4.98) * mm, v(25.29, -5.26) * mm]});
            skFitSpline(sketch, "E239", {"points": [v(25.29, -5.26) * mm, v(25.52, -5.54) * mm, v(25.64, -5.88) * mm, v(25.64, -6.27) * mm]});
            skFitSpline(sketch, "E240", {"points": [v(25.64, -6.27) * mm, v(25.64, -6.7) * mm, v(25.5, -7.06) * mm, v(25.24, -7.36) * mm]});
            skFitSpline(sketch, "E241", {"points": [v(25.24, -7.36) * mm, v(24.97, -7.67) * mm, v(24.55, -7.9) * mm, v(23.99, -8.02) * mm]});
            skLineSegment(sketch, "E242", {"start": v(20.65, -4.7) * mm, "end": v(20.4, -4.7) * mm});
            skLineSegment(sketch, "E243", {"start": v(20.4, -4.7) * mm, "end": v(20.4, -4.52) * mm});
            skLineSegment(sketch, "E244", {"start": v(20.4, -4.52) * mm, "end": v(22.84, -4.52) * mm});
            skFitSpline(sketch, "E245", {"points": [v(25.37, -9.98) * mm, v(25.7, -10.43) * mm, v(25.96, -10.72) * mm, v(26.2, -10.87) * mm]});
            skFitSpline(sketch, "E246", {"points": [v(26.2, -10.87) * mm, v(26.42, -11.02) * mm, v(26.72, -11.11) * mm, v(27.09, -11.15) * mm]});
            skLineSegment(sketch, "E247", {"start": v(23.99, -8.02) * mm, "end": v(25.37, -9.98) * mm});
            skFitSpline(sketch, "E248", {"points": [v(22.3, -7.83) * mm, v(22.37, -7.83) * mm, v(22.43, -7.83) * mm, v(22.47, -7.84) * mm]});
            skFitSpline(sketch, "E249", {"points": [v(22.47, -7.84) * mm, v(22.52, -7.84) * mm, v(22.56, -7.84) * mm, v(22.59, -7.84) * mm]});
            skFitSpline(sketch, "E250", {"points": [v(22.59, -7.84) * mm, v(23.23, -7.84) * mm, v(23.71, -7.7) * mm, v(24.04, -7.42) * mm]});
            skFitSpline(sketch, "E251", {"points": [v(24.04, -7.42) * mm, v(24.36, -7.13) * mm, v(24.53, -6.77) * mm, v(24.53, -6.34) * mm]});
            skFitSpline(sketch, "E252", {"points": [v(24.53, -6.34) * mm, v(24.53, -5.91) * mm, v(24.4, -5.57) * mm, v(24.13, -5.3) * mm]});
            skFitSpline(sketch, "E253", {"points": [v(24.13, -5.3) * mm, v(23.87, -5.03) * mm, v(23.52, -4.9) * mm, v(23.09, -4.9) * mm]});
            skFitSpline(sketch, "E254", {"points": [v(23.09, -4.9) * mm, v(22.9, -4.9) * mm, v(22.64, -4.93) * mm, v(22.3, -5) * mm]});
            skLineSegment(sketch, "E255", {"start": v(27.09, -11.15) * mm, "end": v(27.09, -11.34) * mm});
            skFitSpline(sketch, "E256", {"points": [v(14.9, -2.02) * mm, v(14.32, -1.92) * mm, v(13.14, -1.86) * mm, v(11.13, -1.83) * mm]});
            skFitSpline(sketch, "E257", {"points": [v(11.13, -1.83) * mm, v(9.52, -1.81) * mm, v(7.74, -1.75) * mm, v(7.17, -1.7) * mm]});
            skFitSpline(sketch, "E258", {"points": [v(7.17, -1.7) * mm, v(6.6, -1.64) * mm, v(4.27, -1.58) * mm, v(1.99, -1.55) * mm]});
            skFitSpline(sketch, "E259", {"points": [v(1.99, -1.55) * mm, v(-0.3, -1.52) * mm, v(-2.61, -1.46) * mm, v(-3.17, -1.4) * mm]});
            skFitSpline(sketch, "E260", {"points": [v(-3.17, -1.4) * mm, v(-3.72, -1.35) * mm, v(-6.44, -1.35) * mm, v(-9.2, -1.32) * mm]});
            skFitSpline(sketch, "E261", {"points": [v(-9.2, -1.32) * mm, v(-13.82, -1.6) * mm, v(-16.55, -0.71) * mm, v(-17.96, 0.38) * mm]});
            skFitSpline(sketch, "E262", {"points": [v(-17.96, 0.38) * mm, v(-20.2, 1.65) * mm, v(-20.68, 2.34) * mm, v(-22.94, 2.46) * mm]});
            skFitSpline(sketch, "E263", {"points": [v(-22.94, 2.46) * mm, v(-24.75, 2.45) * mm, v(-25.04, 2.2) * mm, v(-27, 1.44) * mm]});
            skFitSpline(sketch, "E264", {"points": [v(-27, 1.44) * mm, v(-25.87, 2.6) * mm, v(-24.52, 2.92) * mm, v(-22.91, 3.1) * mm]});
            skFitSpline(sketch, "E265", {"points": [v(-22.91, 3.1) * mm, v(-20.46, 3.13) * mm, v(-17.52, 1.15) * mm, v(-15.91, 0.51) * mm]});
            skFitSpline(sketch, "E266", {"points": [v(-15.91, 0.51) * mm, v(-14.3, -0.13) * mm, v(-13.9, -0.04) * mm, v(-12.92, -0.27) * mm]});
            skFitSpline(sketch, "E267", {"points": [v(-12.92, -0.27) * mm, v(-12.71, -0.32) * mm, v(-11.86, -0.4) * mm, v(-11.73, -0.23) * mm]});
            skFitSpline(sketch, "E268", {"points": [v(-11.73, -0.23) * mm, v(-11.65, -0.14) * mm, v(-11.64, 0.21) * mm, v(-11.69, 1.04) * mm]});
            skFitSpline(sketch, "E269", {"points": [v(-11.69, 1.04) * mm, v(-11.75, 2.08) * mm, v(-11.73, 2.24) * mm, v(-11.54, 2.86) * mm]});
            skFitSpline(sketch, "E270", {"points": [v(-11.54, 2.86) * mm, v(-11.42, 3.24) * mm, v(-11.15, 3.88) * mm, v(-10.94, 4.3) * mm]});
            skLineSegment(sketch, "E271", {"start": v(22.3, -5) * mm, "end": v(22.3, -7.83) * mm});
            skFitSpline(sketch, "E272", {"points": [v(-10.7, 5.8) * mm, v(-10.77, 6.22) * mm, v(-10.83, 6.95) * mm, v(-10.82, 7.43) * mm]});
            skFitSpline(sketch, "E273", {"points": [v(-10.82, 7.43) * mm, v(-10.81, 8.27) * mm, v(-10.82, 8.3) * mm, v(-11.02, 8.3) * mm]});
            skFitSpline(sketch, "E274", {"points": [v(-11.02, 8.3) * mm, v(-11.18, 8.3) * mm, v(-11.29, 8.4) * mm, v(-11.43, 8.73) * mm]});
            skFitSpline(sketch, "E275", {"points": [v(-11.43, 8.73) * mm, v(-11.54, 8.96) * mm, v(-11.63, 9.2) * mm, v(-11.63, 9.27) * mm]});
            skFitSpline(sketch, "E276", {"points": [v(-11.63, 9.27) * mm, v(-11.63, 9.42) * mm, v(-11.28, 9.76) * mm, v(-11.04, 9.84) * mm]});
            skFitSpline(sketch, "E277", {"points": [v(-11.04, 9.84) * mm, v(-10.64, 9.98) * mm, v(-10.18, 9.38) * mm, v(-10.28, 8.85) * mm]});
            skFitSpline(sketch, "E278", {"points": [v(-10.28, 8.85) * mm, v(-10.32, 8.64) * mm, v(-10.26, 8.53) * mm, v(-9.87, 8.17) * mm]});
            skFitSpline(sketch, "E279", {"points": [v(-9.87, 8.17) * mm, v(-9.21, 7.56) * mm, v(-8.6, 6.17) * mm, v(-8.76, 5.65) * mm]});
            skFitSpline(sketch, "E280", {"points": [v(-8.76, 5.65) * mm, v(-8.8, 5.56) * mm, v(-8.78, 5.47) * mm, v(-8.72, 5.47) * mm]});
            skFitSpline(sketch, "E281", {"points": [v(-8.72, 5.47) * mm, v(-8.67, 5.47) * mm, v(-8.58, 5.24) * mm, v(-8.51, 4.95) * mm]});
            skFitSpline(sketch, "E282", {"points": [v(-8.51, 4.95) * mm, v(-8.45, 4.66) * mm, v(-8.27, 4.23) * mm, v(-8.11, 4) * mm]});
            skFitSpline(sketch, "E283", {"points": [v(-8.11, 4) * mm, v(-7.96, 3.77) * mm, v(-7.8, 3.45) * mm, v(-7.78, 3.29) * mm]});
            skFitSpline(sketch, "E284", {"points": [v(-7.78, 3.29) * mm, v(-7.72, 3.03) * mm, v(-7.64, 2.96) * mm, v(-7.15, 2.78) * mm]});
            skFitSpline(sketch, "E285", {"points": [v(-7.15, 2.78) * mm, v(-6.84, 2.66) * mm, v(-6.37, 2.56) * mm, v(-6.1, 2.56) * mm]});
            skFitSpline(sketch, "E286", {"points": [v(-6.1, 2.56) * mm, v(-5, 2.55) * mm, v(-4.5, 2.97) * mm, v(-3.72, 4.58) * mm]});
            skFitSpline(sketch, "E287", {"points": [v(-3.72, 4.58) * mm, v(-3.27, 5.5) * mm, v(-3.13, 5.91) * mm, v(-2.96, 6.8) * mm]});
            skFitSpline(sketch, "E288", {"points": [v(-2.96, 6.8) * mm, v(-2.85, 7.4) * mm, v(-2.7, 8.16) * mm, v(-2.62, 8.5) * mm]});
            skFitSpline(sketch, "E289", {"points": [v(-2.62, 8.5) * mm, v(-2.42, 9.5) * mm, v(-2.42, 9.5) * mm, v(-2.94, 9.55) * mm]});
            skFitSpline(sketch, "E290", {"points": [v(-2.94, 9.55) * mm, v(-3.19, 9.57) * mm, v(-3.49, 9.54) * mm, v(-3.62, 9.48) * mm]});
            skFitSpline(sketch, "E291", {"points": [v(-3.62, 9.48) * mm, v(-3.79, 9.4) * mm, v(-3.9, 9.39) * mm, v(-4.07, 9.46) * mm]});
            skFitSpline(sketch, "E292", {"points": [v(-4.07, 9.46) * mm, v(-4.25, 9.55) * mm, v(-4.28, 9.6) * mm, v(-4.23, 9.85) * mm]});
            skFitSpline(sketch, "E293", {"points": [v(-4.23, 9.85) * mm, v(-4.2, 10.01) * mm, v(-4.13, 10.2) * mm, v(-4.09, 10.29) * mm]});
            skFitSpline(sketch, "E294", {"points": [v(-4.09, 10.29) * mm, v(-4, 10.47) * mm, v(-3.05, 10.94) * mm, v(-2.78, 10.94) * mm]});
            skFitSpline(sketch, "E295", {"points": [v(-2.78, 10.94) * mm, v(-2.68, 10.94) * mm, v(-2.43, 11.03) * mm, v(-2.23, 11.13) * mm]});
            skFitSpline(sketch, "E296", {"points": [v(-2.23, 11.13) * mm, v(-1.48, 11.52) * mm, v(-1.37, 11.5) * mm, v(-0.76, 10.73) * mm]});
            skFitSpline(sketch, "E297", {"points": [v(-0.76, 10.73) * mm, v(-0.1, 9.91) * mm, v(0.8, 9.1) * mm, v(1.27, 8.9) * mm]});
            skFitSpline(sketch, "E298", {"points": [v(1.27, 8.9) * mm, v(2.05, 8.56) * mm, v(3.55, 8.79) * mm, v(4.47, 9.4) * mm]});
            skFitSpline(sketch, "E299", {"points": [v(4.47, 9.4) * mm, v(5.16, 9.85) * mm, v(6.18, 10.91) * mm, v(6.25, 11.25) * mm]});
            skFitSpline(sketch, "E300", {"points": [v(6.25, 11.25) * mm, v(6.32, 11.6) * mm, v(6.57, 11.58) * mm, v(6.89, 11.2) * mm]});
            skFitSpline(sketch, "E301", {"points": [v(6.89, 11.2) * mm, v(7.1, 10.96) * mm, v(7.17, 10.92) * mm, v(7.3, 11.01) * mm]});
            skFitSpline(sketch, "E302", {"points": [v(7.3, 11.01) * mm, v(7.42, 11.08) * mm, v(7.87, 11.1) * mm, v(8.7, 11.06) * mm]});
            skFitSpline(sketch, "E303", {"points": [v(8.7, 11.06) * mm, v(9.75, 11.02) * mm, v(9.92, 11.03) * mm, v(10.03, 11.16) * mm]});
            skFitSpline(sketch, "E304", {"points": [v(10.03, 11.16) * mm, v(10.27, 11.45) * mm, v(10.7, 11.3) * mm, v(10.7, 10.92) * mm]});
            skFitSpline(sketch, "E305", {"points": [v(10.7, 10.92) * mm, v(10.7, 10.83) * mm, v(10.8, 10.7) * mm, v(10.93, 10.65) * mm]});
            skFitSpline(sketch, "E306", {"points": [v(10.93, 10.65) * mm, v(11.05, 10.6) * mm, v(11.22, 10.4) * mm, v(11.3, 10.22) * mm]});
            skFitSpline(sketch, "E307", {"points": [v(11.3, 10.22) * mm, v(11.4, 10.04) * mm, v(11.64, 9.7) * mm, v(11.87, 9.45) * mm]});
            skFitSpline(sketch, "E308", {"points": [v(11.87, 9.45) * mm, v(12.52, 8.74) * mm, v(12.96, 8.08) * mm, v(13.3, 7.28) * mm]});
            skFitSpline(sketch, "E309", {"points": [v(13.3, 7.28) * mm, v(13.57, 6.66) * mm, v(13.64, 6.35) * mm, v(13.72, 5.44) * mm]});
            skFitSpline(sketch, "E310", {"points": [v(13.72, 5.44) * mm, v(13.78, 4.71) * mm, v(13.88, 4.21) * mm, v(14, 3.98) * mm]});
            skFitSpline(sketch, "E311", {"points": [v(14, 3.98) * mm, v(14.09, 3.8) * mm, v(14.2, 3.44) * mm, v(14.23, 3.2) * mm]});
            skFitSpline(sketch, "E312", {"points": [v(14.23, 3.2) * mm, v(14.26, 2.97) * mm, v(14.37, 2.65) * mm, v(14.48, 2.48) * mm]});
            skFitSpline(sketch, "E313", {"points": [v(14.48, 2.48) * mm, v(14.63, 2.22) * mm, v(14.66, 2.02) * mm, v(14.65, 1.02) * mm]});
            skFitSpline(sketch, "E314", {"points": [v(14.65, 1.02) * mm, v(14.64, 0.39) * mm, v(14.69, -0.4) * mm, v(14.75, -0.7) * mm]});
            skLineSegment(sketch, "E315", {"start": v(-10.94, 4.3) * mm, "end": v(-10.56, 5.05) * mm});
            skLineSegment(sketch, "E316", {"start": v(-10.56, 5.05) * mm, "end": v(-10.7, 5.8) * mm});
            skFitSpline(sketch, "E317", {"points": [v(15.55, -1.29) * mm, v(15.92, -1.29) * mm, v(16.68, -1.32) * mm, v(17.24, -1.36) * mm]});
            skFitSpline(sketch, "E318", {"points": [v(17.24, -1.36) * mm, v(17.95, -1.41) * mm, v(18.5, -1.4) * mm, v(19.08, -1.3) * mm]});
            skFitSpline(sketch, "E319", {"points": [v(19.08, -1.3) * mm, v(19.83, -1.2) * mm, v(20.08, -1.09) * mm, v(22.26, 0.02) * mm]});
            skFitSpline(sketch, "E320", {"points": [v(22.26, 0.02) * mm, v(24.46, 1.13) * mm, v(26.33, 1.88) * mm, v(26.65, 1.78) * mm]});
            skFitSpline(sketch, "E321", {"points": [v(26.65, 1.78) * mm, v(25.57, 1.15) * mm, v(25.16, 0.92) * mm, v(24.84, 0.82) * mm]});
            skFitSpline(sketch, "E322", {"points": [v(24.84, 0.82) * mm, v(24.03, 0.45) * mm, v(23.12, -0.07) * mm, v(21.21, -1.02) * mm]});
            skFitSpline(sketch, "E323", {"points": [v(21.21, -1.02) * mm, v(18.99, -2.13) * mm, v(18.7, -1.93) * mm, v(17.93, -2.06) * mm]});
            skFitSpline(sketch, "E324", {"points": [v(17.93, -2.06) * mm, v(17.11, -2.06) * mm, v(15.47, -2.05) * mm, v(14.9, -2.02) * mm]});
            skLineSegment(sketch, "E325", {"start": v(14.75, -0.7) * mm, "end": v(14.87, -1.29) * mm});
            skLineSegment(sketch, "E326", {"start": v(14.87, -1.29) * mm, "end": v(15.55, -1.29) * mm});
            skFitSpline(sketch, "E327", {"points": [v(14.33, -1.08) * mm, v(14.48, -0.53) * mm, v(14.37, 0.67) * mm, v(14.1, 1.54) * mm]});
            skFitSpline(sketch, "E328", {"points": [v(14.1, 1.54) * mm, v(13.78, 2.6) * mm, v(13.23, 3.73) * mm, v(12.98, 3.87) * mm]});
            skFitSpline(sketch, "E329", {"points": [v(12.98, 3.87) * mm, v(12.88, 3.92) * mm, v(12.73, 4.11) * mm, v(12.65, 4.3) * mm]});
            skFitSpline(sketch, "E330", {"points": [v(12.65, 4.3) * mm, v(12.56, 4.48) * mm, v(12.45, 4.63) * mm, v(12.4, 4.63) * mm]});
            skFitSpline(sketch, "E331", {"points": [v(12.4, 4.63) * mm, v(12.21, 4.63) * mm, v(12.3, 3.24) * mm, v(12.53, 2.5) * mm]});
            skLineSegment(sketch, "E332", {"start": v(14.9, -2.02) * mm, "end": v(14.9, -2.02) * mm});
            skFitSpline(sketch, "E333", {"points": [v(12.16, 0.55) * mm, v(11.84, -0.14) * mm, v(11.54, -0.81) * mm, v(11.5, -0.95) * mm]});
            skLineSegment(sketch, "E334", {"start": v(12.53, 2.5) * mm, "end": v(12.76, 1.79) * mm});
            skLineSegment(sketch, "E335", {"start": v(12.76, 1.79) * mm, "end": v(12.16, 0.55) * mm});
            skFitSpline(sketch, "E336", {"points": [v(12.09, -1.24) * mm, v(12.44, -1.25) * mm, v(13.08, -1.27) * mm, v(13.5, -1.27) * mm]});
            skFitSpline(sketch, "E337", {"points": [v(13.5, -1.27) * mm, v(14.2, -1.26) * mm, v(14.28, -1.24) * mm, v(14.33, -1.08) * mm]});
            skLineSegment(sketch, "E338", {"start": v(11.5, -0.95) * mm, "end": v(11.44, -1.2) * mm});
            skLineSegment(sketch, "E339", {"start": v(11.44, -1.2) * mm, "end": v(12.09, -1.24) * mm});
            skFitSpline(sketch, "E340", {"points": [v(11.07, -1.1) * mm, v(11.05, -1.03) * mm, v(11.12, -0.87) * mm, v(11.21, -0.73) * mm]});
            skFitSpline(sketch, "E341", {"points": [v(11.21, -0.73) * mm, v(11.47, -0.34) * mm, v(11.83, 0.78) * mm, v(11.9, 1.4) * mm]});
            skFitSpline(sketch, "E342", {"points": [v(11.9, 1.4) * mm, v(11.97, 2.1) * mm, v(11.67, 3.31) * mm, v(11.34, 3.67) * mm]});
            skFitSpline(sketch, "E343", {"points": [v(11.34, 3.67) * mm, v(10.94, 4.1) * mm, v(10.69, 4.53) * mm, v(10.74, 4.68) * mm]});
            skFitSpline(sketch, "E344", {"points": [v(10.74, 4.68) * mm, v(10.86, 4.99) * mm, v(10.68, 5.4) * mm, v(10.39, 5.52) * mm]});
            skFitSpline(sketch, "E345", {"points": [v(10.39, 5.52) * mm, v(10.06, 5.65) * mm, v(9.25, 5.63) * mm, v(8.68, 5.49) * mm]});
            skFitSpline(sketch, "E346", {"points": [v(8.68, 5.49) * mm, v(8.47, 5.43) * mm, v(8.13, 5.35) * mm, v(7.93, 5.3) * mm]});
            skFitSpline(sketch, "E347", {"points": [v(7.93, 5.3) * mm, v(7.72, 5.26) * mm, v(7.44, 5.17) * mm, v(7.31, 5.1) * mm]});
            skFitSpline(sketch, "E348", {"points": [v(7.31, 5.1) * mm, v(7.19, 5.03) * mm, v(6.91, 4.95) * mm, v(6.7, 4.93) * mm]});
            skFitSpline(sketch, "E349", {"points": [v(6.7, 4.93) * mm, v(6.5, 4.9) * mm, v(6.32, 4.88) * mm, v(6.31, 4.88) * mm]});
            skFitSpline(sketch, "E350", {"points": [v(6.31, 4.88) * mm, v(6.3, 4.87) * mm, v(6.39, 4.4) * mm, v(6.5, 3.83) * mm]});
            skFitSpline(sketch, "E351", {"points": [v(6.5, 3.83) * mm, v(6.6, 3.16) * mm, v(6.67, 2.42) * mm, v(6.66, 1.75) * mm]});
            skFitSpline(sketch, "E352", {"points": [v(6.66, 1.75) * mm, v(6.65, 1.18) * mm, v(6.67, 0.37) * mm, v(6.7, -0.06) * mm]});
            skFitSpline(sketch, "E353", {"points": [v(7.08, -0.93) * mm, v(7.25, -1) * mm, v(7.7, -1.04) * mm, v(8.08, -1.03) * mm]});
            skFitSpline(sketch, "E354", {"points": [v(8.08, -1.03) * mm, v(9.02, -1.03) * mm, v(10.63, -1.11) * mm, v(10.7, -1.17) * mm]});
            skFitSpline(sketch, "E355", {"points": [v(10.7, -1.17) * mm, v(10.79, -1.27) * mm, v(11.09, -1.21) * mm, v(11.07, -1.1) * mm]});
            skLineSegment(sketch, "E356", {"start": v(6.7, -0.06) * mm, "end": v(6.76, -0.83) * mm});
            skLineSegment(sketch, "E357", {"start": v(6.76, -0.83) * mm, "end": v(7.08, -0.93) * mm});
            skFitSpline(sketch, "E358", {"points": [v(6.18, -0.75) * mm, v(6.32, -0.48) * mm, v(6.3, 1.06) * mm, v(6.15, 1.43) * mm]});
            skFitSpline(sketch, "E359", {"points": [v(6.15, 1.43) * mm, v(6.02, 1.99) * mm, v(6.05, 2.04) * mm, v(6.06, 2.08) * mm]});
            skFitSpline(sketch, "E360", {"points": [v(6.06, 2.08) * mm, v(6.1, 2.23) * mm, v(6.1, 2.24) * mm, v(6.08, 2.33) * mm]});
            skFitSpline(sketch, "E361", {"points": [v(6.08, 2.33) * mm, v(6.06, 2.43) * mm, v(5.94, 2.97) * mm, v(5.85, 3.54) * mm]});
            skFitSpline(sketch, "E362", {"points": [v(5.85, 3.54) * mm, v(5.66, 4.84) * mm, v(5.64, 4.9) * mm, v(5.43, 4.9) * mm]});
            skFitSpline(sketch, "E363", {"points": [v(5.43, 4.9) * mm, v(5.14, 4.9) * mm, v(4.82, 4.57) * mm, v(4.23, 3.62) * mm]});
            skFitSpline(sketch, "E364", {"points": [v(4.23, 3.62) * mm, v(3.64, 2.66) * mm, v(3.17, 1.48) * mm, v(3.16, 0.93) * mm]});
            skFitSpline(sketch, "E365", {"points": [v(3.16, 0.93) * mm, v(3.16, 0.76) * mm, v(3.1, 0.32) * mm, v(3.03, -0.04) * mm]});
            skFitSpline(sketch, "E366", {"points": [v(3.03, -0.04) * mm, v(2.96, -0.4) * mm, v(2.92, -0.72) * mm, v(2.94, -0.74) * mm]});
            skFitSpline(sketch, "E367", {"points": [v(2.94, -0.74) * mm, v(2.98, -0.79) * mm, v(4.56, -0.9) * mm, v(5.5, -0.92) * mm]});
            skFitSpline(sketch, "E368", {"points": [v(5.5, -0.92) * mm, v(5.99, -0.93) * mm, v(6.1, -0.9) * mm, v(6.18, -0.75) * mm]});
            skFitSpline(sketch, "E369", {"points": [v(2.55, -0.4) * mm, v(2.59, -0.2) * mm, v(2.68, 0.25) * mm, v(2.75, 0.61) * mm]});
            skFitSpline(sketch, "E370", {"points": [v(2.75, 0.61) * mm, v(2.84, 1.02) * mm, v(2.87, 1.45) * mm, v(2.83, 1.76) * mm]});
            skFitSpline(sketch, "E371", {"points": [v(2.83, 1.76) * mm, v(2.76, 2.3) * mm, v(2.75, 2.26) * mm, v(3.44, 3.5) * mm]});
            skFitSpline(sketch, "E372", {"points": [v(3.44, 3.5) * mm, v(3.66, 3.88) * mm, v(3.92, 4.45) * mm, v(4.03, 4.76) * mm]});
            skFitSpline(sketch, "E373", {"points": [v(4.03, 4.76) * mm, v(4.2, 5.3) * mm, v(4.2, 5.34) * mm, v(4.05, 5.74) * mm]});
            skFitSpline(sketch, "E374", {"points": [v(4.05, 5.74) * mm, v(3.87, 6.23) * mm, v(3.46, 6.7) * mm, v(3.21, 6.7) * mm]});
            skFitSpline(sketch, "E375", {"points": [v(3.21, 6.7) * mm, v(2.83, 6.7) * mm, v(1.5, 7.02) * mm, v(1.05, 7.22) * mm]});
            skFitSpline(sketch, "E376", {"points": [v(1.05, 7.22) * mm, v(0.58, 7.43) * mm, v(-0.12, 7.95) * mm, v(-1.03, 8.8) * mm]});
            skFitSpline(sketch, "E377", {"points": [v(-1.03, 8.8) * mm, v(-1.29, 9.03) * mm, v(-1.68, 9.3) * mm, v(-1.9, 9.37) * mm]});
            skFitSpline(sketch, "E378", {"points": [v(-1.9, 9.37) * mm, v(-2.36, 9.53) * mm, v(-2.29, 9.63) * mm, v(-2.49, 8.5) * mm]});
            skFitSpline(sketch, "E379", {"points": [v(-2.49, 8.5) * mm, v(-2.88, 6.27) * mm, v(-3.08, 5.5) * mm, v(-3.58, 4.49) * mm]});
            skFitSpline(sketch, "E380", {"points": [v(-3.58, 4.49) * mm, v(-3.9, 3.84) * mm, v(-4.4, 3.07) * mm, v(-4.65, 2.9) * mm]});
            skFitSpline(sketch, "E381", {"points": [v(-4.65, 2.9) * mm, v(-4.93, 2.64) * mm, v(-5.26, 2.5) * mm, v(-5.6, 2.46) * mm]});
            skFitSpline(sketch, "E382", {"points": [v(-5.6, 2.46) * mm, v(-5.93, 2.36) * mm, v(-6.77, 2.49) * mm, v(-6.93, 2.54) * mm]});
            skFitSpline(sketch, "E383", {"points": [v(-6.93, 2.54) * mm, v(-7.28, 2.67) * mm, v(-7.25, 2.68) * mm, v(-7.33, 2.28) * mm]});
            skFitSpline(sketch, "E384", {"points": [v(-7.33, 2.28) * mm, v(-7.38, 2.03) * mm, v(-7.36, 1.96) * mm, v(-7.22, 1.93) * mm]});
            skFitSpline(sketch, "E385", {"points": [v(-7.22, 1.93) * mm, v(-6.97, 1.86) * mm, v(-6.79, 1.53) * mm, v(-6.92, 1.37) * mm]});
            skFitSpline(sketch, "E386", {"points": [v(-6.92, 1.37) * mm, v(-7, 1.28) * mm, v(-7, 1.2) * mm, v(-6.92, 1.04) * mm]});
            skFitSpline(sketch, "E387", {"points": [v(-6.92, 1.04) * mm, v(-6.68, 0.6) * mm, v(-7.07, 0.43) * mm, v(-7.59, 0.74) * mm]});
            skFitSpline(sketch, "E388", {"points": [v(-7.59, 0.74) * mm, v(-7.85, 0.89) * mm, v(-7.87, 0.89) * mm, v(-8.02, 0.74) * mm]});
            skFitSpline(sketch, "E389", {"points": [v(-8.02, 0.74) * mm, v(-8.07, 0.63) * mm, v(-8.06, 0.54) * mm, v(-8.03, 0.47) * mm]});
            skFitSpline(sketch, "E390", {"points": [v(-8.03, 0.47) * mm, v(-7.95, 0.28) * mm, v(-7.79, 0.14) * mm, v(-7.64, -0.05) * mm]});
            skFitSpline(sketch, "E391", {"points": [v(-7.64, -0.05) * mm, v(-7.44, -0.35) * mm, v(-7.3, -0.46) * mm, v(-7.05, -0.5) * mm]});
            skFitSpline(sketch, "E392", {"points": [v(-7.05, -0.5) * mm, v(-6.87, -0.54) * mm, v(-5.31, -0.59) * mm, v(-3.6, -0.61) * mm]});
            skFitSpline(sketch, "E393", {"points": [v(-3.6, -0.61) * mm, v(-1.88, -0.63) * mm, v(-0.54, -0.7) * mm, v(-0.43, -0.7) * mm]});
            skFitSpline(sketch, "E394", {"points": [v(-0.43, -0.7) * mm, v(-0.14, -0.71) * mm, v(-0.1, -0.7) * mm, v(0.23, -0.71) * mm]});
            skFitSpline(sketch, "E395", {"points": [v(0.23, -0.71) * mm, v(0.44, -0.74) * mm, v(1.26, -0.74) * mm, v(1.35, -0.74) * mm]});
            skLineSegment(sketch, "E396", {"start": v(1.35, -0.74) * mm, "end": v(2.5, -0.76) * mm});
            skLineSegment(sketch, "E397", {"start": v(2.5, -0.76) * mm, "end": v(2.55, -0.4) * mm});
            skFitSpline(sketch, "E398", {"points": [v(-8.92, -0.48) * mm, v(-8.16, -0.44) * mm, v(-8.06, -0.35) * mm, v(-8.25, 0) * mm]});
            skFitSpline(sketch, "E399", {"points": [v(-8.25, 0) * mm, v(-8.28, 0.08) * mm, v(-8.33, 0.21) * mm, v(-8.43, 0.4) * mm]});
            skFitSpline(sketch, "E400", {"points": [v(-8.43, 0.4) * mm, v(-8.51, 0.5) * mm, v(-8.55, 0.54) * mm, v(-8.66, 0.57) * mm]});
            skFitSpline(sketch, "E401", {"points": [v(-8.66, 0.57) * mm, v(-8.8, 0.61) * mm, v(-8.93, 0.65) * mm, v(-9, 0.76) * mm]});
            skFitSpline(sketch, "E402", {"points": [v(-9, 0.76) * mm, v(-9.07, 0.91) * mm, v(-9.2, 0.95) * mm, v(-9.55, 0.95) * mm]});
            skFitSpline(sketch, "E403", {"points": [v(-9.55, 0.95) * mm, v(-9.8, 0.95) * mm, v(-10.18, 1.01) * mm, v(-10.4, 1.09) * mm]});
            skFitSpline(sketch, "E404", {"points": [v(-10.4, 1.09) * mm, v(-10.76, 1.22) * mm, v(-10.8, 1.21) * mm, v(-10.85, 1.07) * mm]});
            skFitSpline(sketch, "E405", {"points": [v(-10.85, 1.07) * mm, v(-10.88, 0.98) * mm, v(-10.97, 0.83) * mm, v(-11.04, 0.75) * mm]});
            skFitSpline(sketch, "E406", {"points": [v(-11.04, 0.75) * mm, v(-11.12, 0.65) * mm, v(-11.16, 0.43) * mm, v(-11.14, 0.14) * mm]});
            skFitSpline(sketch, "E407", {"points": [v(-11.14, 0.14) * mm, v(-11.12, -0.26) * mm, v(-11.09, -0.32) * mm, v(-10.85, -0.38) * mm]});
            skFitSpline(sketch, "E408", {"points": [v(-10.85, -0.38) * mm, v(-10.7, -0.42) * mm, v(-10.53, -0.42) * mm, v(-10.41, -0.43) * mm]});
            skFitSpline(sketch, "E409", {"points": [v(-10.41, -0.43) * mm, v(-10.16, -0.45) * mm, v(-9.93, -0.5) * mm, v(-9.74, -0.5) * mm]});
            skFitSpline(sketch, "E410", {"points": [v(-9.74, -0.5) * mm, v(-9.65, -0.51) * mm, v(-9.6, -0.5) * mm, v(-9.5, -0.5) * mm]});
            skFitSpline(sketch, "E411", {"points": [v(-9.5, -0.5) * mm, v(-9.4, -0.49) * mm, v(-9.3, -0.5) * mm, v(-8.92, -0.48) * mm]});
            skLineSegment(sketch, "E412", {"start": v(1.35, -0.74) * mm, "end": v(1.35, -0.74) * mm});
            skLineSegment(sketch, "E413", {"start": v(-8.92, -0.48) * mm, "end": v(-8.92, -0.48) * mm});
            skSolve(sketch);
        }
        {
            var Q0;
            Q0 = qSketchRegion(id + "F0", true);
            extrude(context, id + "F1", {"entities" : qUnion([Q0]), "depth" : 2 * mm, "offsetDistance" : 25 * mm});
        }
        {
            var Q0;
            Q0=makeQuery(id+"F1.opExtrude","CAP_FACE",FACE,{"disambiguationData":[OSD([sQuery(id+"F0.wireOp",EDGE,"E256"),sQuery(id+"F0.wireOp",EDGE,"E257"),sQuery(id+"F0.wireOp",EDGE,"E258"),sQuery(id+"F0.wireOp",EDGE,"E259"),sQuery(id+"F0.wireOp",EDGE,"E260"),sQuery(id+"F0.wireOp",EDGE,"E261"),sQuery(id+"F0.wireOp",EDGE,"E262"),sQuery(id+"F0.wireOp",EDGE,"E263"),sQuery(id+"F0.wireOp",EDGE,"E264"),sQuery(id+"F0.wireOp",EDGE,"E265"),sQuery(id+"F0.wireOp",EDGE,"E266"),sQuery(id+"F0.wireOp",EDGE,"E267"),sQuery(id+"F0.wireOp",EDGE,"E268"),sQuery(id+"F0.wireOp",EDGE,"E269"),sQuery(id+"F0.wireOp",EDGE,"E270"),sQuery(id+"F0.wireOp",EDGE,"E272"),sQuery(id+"F0.wireOp",EDGE,"E273"),sQuery(id+"F0.wireOp",EDGE,"E274"),sQuery(id+"F0.wireOp",EDGE,"E275"),sQuery(id+"F0.wireOp",EDGE,"E276"),sQuery(id+"F0.wireOp",EDGE,"E277"),sQuery(id+"F0.wireOp",EDGE,"E278"),sQuery(id+"F0.wireOp",EDGE,"E279"),sQuery(id+"F0.wireOp",EDGE,"E280"),sQuery(id+"F0.wireOp",EDGE,"E281"),sQuery(id+"F0.wireOp",EDGE,"E282"),sQuery(id+"F0.wireOp",EDGE,"E283"),sQuery(id+"F0.wireOp",EDGE,"E284"),sQuery(id+"F0.wireOp",EDGE,"E285"),sQuery(id+"F0.wireOp",EDGE,"E286"),sQuery(id+"F0.wireOp",EDGE,"E287"),sQuery(id+"F0.wireOp",EDGE,"E288"),sQuery(id+"F0.wireOp",EDGE,"E289"),sQuery(id+"F0.wireOp",EDGE,"E290"),sQuery(id+"F0.wireOp",EDGE,"E291"),sQuery(id+"F0.wireOp",EDGE,"E292"),sQuery(id+"F0.wireOp",EDGE,"E293"),sQuery(id+"F0.wireOp",EDGE,"E294"),sQuery(id+"F0.wireOp",EDGE,"E295"),sQuery(id+"F0.wireOp",EDGE,"E296"),sQuery(id+"F0.wireOp",EDGE,"E297"),sQuery(id+"F0.wireOp",EDGE,"E298"),sQuery(id+"F0.wireOp",EDGE,"E299"),sQuery(id+"F0.wireOp",EDGE,"E300"),sQuery(id+"F0.wireOp",EDGE,"E301"),sQuery(id+"F0.wireOp",EDGE,"E302"),sQuery(id+"F0.wireOp",EDGE,"E303"),sQuery(id+"F0.wireOp",EDGE,"E304"),sQuery(id+"F0.wireOp",EDGE,"E305"),sQuery(id+"F0.wireOp",EDGE,"E306"),sQuery(id+"F0.wireOp",EDGE,"E307"),sQuery(id+"F0.wireOp",EDGE,"E308"),sQuery(id+"F0.wireOp",EDGE,"E309"),sQuery(id+"F0.wireOp",EDGE,"E310"),sQuery(id+"F0.wireOp",EDGE,"E311"),sQuery(id+"F0.wireOp",EDGE,"E312"),sQuery(id+"F0.wireOp",EDGE,"E313"),sQuery(id+"F0.wireOp",EDGE,"E314"),sQuery(id+"F0.wireOp",EDGE,"E315"),sQuery(id+"F0.wireOp",EDGE,"E316"),sQuery(id+"F0.wireOp",EDGE,"E317"),sQuery(id+"F0.wireOp",EDGE,"E318"),sQuery(id+"F0.wireOp",EDGE,"E319"),sQuery(id+"F0.wireOp",EDGE,"E320"),sQuery(id+"F0.wireOp",EDGE,"E321"),sQuery(id+"F0.wireOp",EDGE,"E322"),sQuery(id+"F0.wireOp",EDGE,"E323"),sQuery(id+"F0.wireOp",EDGE,"E324"),sQuery(id+"F0.wireOp",EDGE,"E325"),sQuery(id+"F0.wireOp",EDGE,"E326"),sQuery(id+"F0.wireOp",EDGE,"E327"),sQuery(id+"F0.wireOp",EDGE,"E328"),sQuery(id+"F0.wireOp",EDGE,"E329"),sQuery(id+"F0.wireOp",EDGE,"E330"),sQuery(id+"F0.wireOp",EDGE,"E331"),sQuery(id+"F0.wireOp",EDGE,"E333"),sQuery(id+"F0.wireOp",EDGE,"E334"),sQuery(id+"F0.wireOp",EDGE,"E335"),sQuery(id+"F0.wireOp",EDGE,"E336"),sQuery(id+"F0.wireOp",EDGE,"E337"),sQuery(id+"F0.wireOp",EDGE,"E338"),sQuery(id+"F0.wireOp",EDGE,"E339"),sQuery(id+"F0.wireOp",EDGE,"E340"),sQuery(id+"F0.wireOp",EDGE,"E341"),sQuery(id+"F0.wireOp",EDGE,"E342"),sQuery(id+"F0.wireOp",EDGE,"E343"),sQuery(id+"F0.wireOp",EDGE,"E344"),sQuery(id+"F0.wireOp",EDGE,"E345"),sQuery(id+"F0.wireOp",EDGE,"E346"),sQuery(id+"F0.wireOp",EDGE,"E347"),sQuery(id+"F0.wireOp",EDGE,"E348"),sQuery(id+"F0.wireOp",EDGE,"E349"),sQuery(id+"F0.wireOp",EDGE,"E350"),sQuery(id+"F0.wireOp",EDGE,"E351"),sQuery(id+"F0.wireOp",EDGE,"E352"),sQuery(id+"F0.wireOp",EDGE,"E353"),sQuery(id+"F0.wireOp",EDGE,"E354"),sQuery(id+"F0.wireOp",EDGE,"E355"),sQuery(id+"F0.wireOp",EDGE,"E356"),sQuery(id+"F0.wireOp",EDGE,"E357"),sQuery(id+"F0.wireOp",EDGE,"E358"),sQuery(id+"F0.wireOp",EDGE,"E359"),sQuery(id+"F0.wireOp",EDGE,"E360"),sQuery(id+"F0.wireOp",EDGE,"E361"),sQuery(id+"F0.wireOp",EDGE,"E362"),sQuery(id+"F0.wireOp",EDGE,"E363"),sQuery(id+"F0.wireOp",EDGE,"E364"),sQuery(id+"F0.wireOp",EDGE,"E365"),sQuery(id+"F0.wireOp",EDGE,"E366"),sQuery(id+"F0.wireOp",EDGE,"E367"),sQuery(id+"F0.wireOp",EDGE,"E368"),sQuery(id+"F0.wireOp",EDGE,"E369"),sQuery(id+"F0.wireOp",EDGE,"E370"),sQuery(id+"F0.wireOp",EDGE,"E371"),sQuery(id+"F0.wireOp",EDGE,"E372"),sQuery(id+"F0.wireOp",EDGE,"E373"),sQuery(id+"F0.wireOp",EDGE,"E374"),sQuery(id+"F0.wireOp",EDGE,"E375"),sQuery(id+"F0.wireOp",EDGE,"E376"),sQuery(id+"F0.wireOp",EDGE,"E377"),sQuery(id+"F0.wireOp",EDGE,"E378"),sQuery(id+"F0.wireOp",EDGE,"E379"),sQuery(id+"F0.wireOp",EDGE,"E380"),sQuery(id+"F0.wireOp",EDGE,"E381"),sQuery(id+"F0.wireOp",EDGE,"E382"),sQuery(id+"F0.wireOp",EDGE,"E383"),sQuery(id+"F0.wireOp",EDGE,"E384"),sQuery(id+"F0.wireOp",EDGE,"E385"),sQuery(id+"F0.wireOp",EDGE,"E386"),sQuery(id+"F0.wireOp",EDGE,"E387"),sQuery(id+"F0.wireOp",EDGE,"E388"),sQuery(id+"F0.wireOp",EDGE,"E389"),sQuery(id+"F0.wireOp",EDGE,"E390"),sQuery(id+"F0.wireOp",EDGE,"E391"),sQuery(id+"F0.wireOp",EDGE,"E392"),sQuery(id+"F0.wireOp",EDGE,"E393"),sQuery(id+"F0.wireOp",EDGE,"E394"),sQuery(id+"F0.wireOp",EDGE,"E395"),sQuery(id+"F0.wireOp",EDGE,"E396"),sQuery(id+"F0.wireOp",EDGE,"E397"),sQuery(id+"F0.wireOp",EDGE,"E398"),sQuery(id+"F0.wireOp",EDGE,"E399"),sQuery(id+"F0.wireOp",EDGE,"E400"),sQuery(id+"F0.wireOp",EDGE,"E401"),sQuery(id+"F0.wireOp",EDGE,"E402"),sQuery(id+"F0.wireOp",EDGE,"E403"),sQuery(id+"F0.wireOp",EDGE,"E404"),sQuery(id+"F0.wireOp",EDGE,"E405"),sQuery(id+"F0.wireOp",EDGE,"E406"),sQuery(id+"F0.wireOp",EDGE,"E407"),sQuery(id+"F0.wireOp",EDGE,"E408"),sQuery(id+"F0.wireOp",EDGE,"E409"),sQuery(id+"F0.wireOp",EDGE,"E410"),sQuery(id+"F0.wireOp",EDGE,"E411"),sQuery(id+"F0.wireOp",EDGE,"E412")])],"isStart":true});
            var sketch = newSketch(context, id + "F2", { "sketchPlane" : qUnion([Q0])});
            skLineSegment(sketch, "E414.bottom", {"start": v(-27.65, 12.48) * mm, "end": v(28, 12.48) * mm});
            skLineSegment(sketch, "E414.top", {"start": v(-27.65, -12.34) * mm, "end": v(28, -12.34) * mm});
            skLineSegment(sketch, "E414.left", {"start": v(-27.65, 12.48) * mm, "end": v(-27.65, -12.34) * mm});
            skLineSegment(sketch, "E414.right", {"start": v(28, 12.48) * mm, "end": v(28, -12.34) * mm});
            skSolve(sketch);
        }
        {
            var Q0;
            Q0 = qSketchRegion(id + "F2", true);
            extrude(context, id + "F3", {"entities" : qUnion([Q0]), "operationType" : NewBodyOperationType.ADD, "depth" : 1 * mm, "offsetDistance" : 25 * mm});
        }
    });
